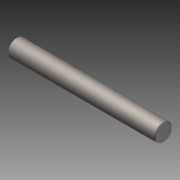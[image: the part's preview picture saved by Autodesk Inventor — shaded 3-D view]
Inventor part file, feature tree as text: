
AUTODESK INVENTOR PART (.ipt)
format: ipt  version: 2015 (Build 190159000, 159)  size: 101,888 bytes
history: native  units: in
note: dims shown in document units (in); Inventor stores cm internally (conversion verified against a paired STEP export)
features: revolve x1, other x1, imported_body x1
ambient origin geometry x8: Origin, YZ Plane, XZ Plane, XY Plane, X Axis, Y Axis, Z Axis, Center Point
bodies: Body1 (feature_tree)
feature tree (3):
  revolve  "Revolve1"  [1 undecoded]
  other  "tetrix_736466_roller_axle1"
  imported_body  "Base1"
note: 1 required parameter value undecoded (feature->parameter linkage not recoverable at this tier; creation-order binding heuristic only, values carry confidence <= 0.55)
